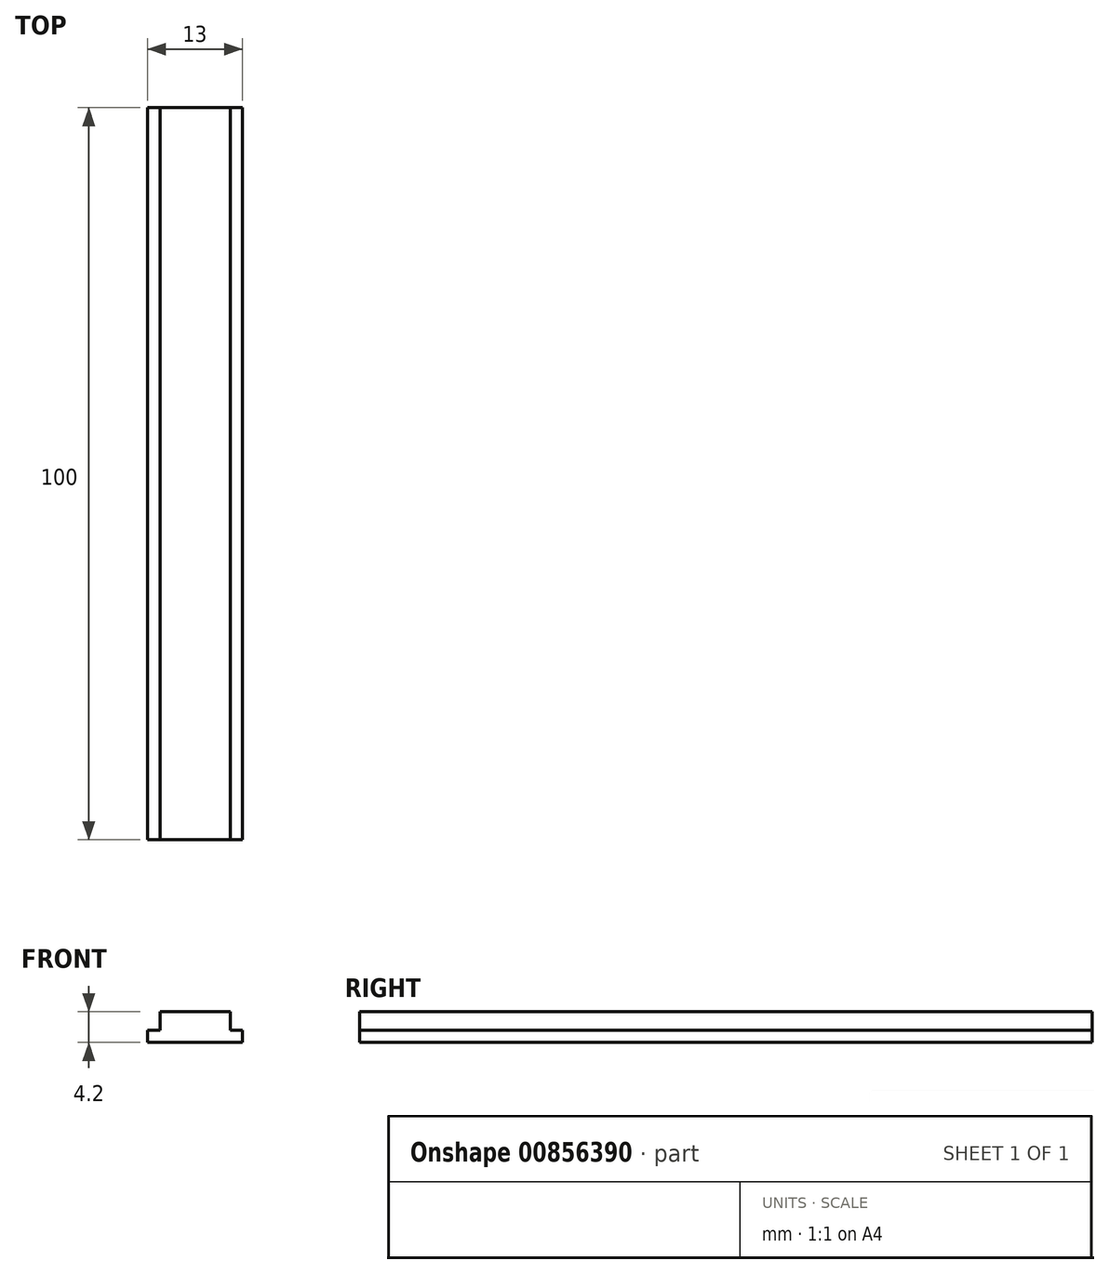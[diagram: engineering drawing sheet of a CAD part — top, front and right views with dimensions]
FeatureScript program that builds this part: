
annotation { "Feature Type Name" : "Feature", "Feature Type Description" : "" }
export const myFeature = defineFeature(function(context is Context, id is Id, definition is map)
    precondition{}
    {
        {
            var Q0;
            Q0=qCreatedBy(makeId("Front.planeOp"),FACE);
            var sketch = newSketch(context, id + "F0", { "sketchPlane" : qUnion([Q0])});
            skLineSegment(sketch, "E0", {"start": v(0.55, 2.47) * mm, "end": v(7.05, 2.47) * mm});
            skLineSegment(sketch, "E1", {"start": v(7.05, 2.47) * mm, "end": v(7.05, 4.17) * mm});
            skLineSegment(sketch, "E2", {"start": v(7.05, 4.17) * mm, "end": v(5.35, 4.17) * mm});
            skLineSegment(sketch, "E3", {"start": v(5.35, 4.17) * mm, "end": v(5.35, 6.67) * mm});
            skLineSegment(sketch, "E4", {"start": v(5.35, 6.67) * mm, "end": v(0.55, 6.67) * mm});
            skLineSegment(sketch, "E5.MirrorCS", {"start": v(-4.25, 6.67) * mm, "end": v(0.55, 6.67) * mm});
            skLineSegment(sketch, "E6.MirrorCS", {"start": v(-4.25, 4.17) * mm, "end": v(-4.25, 6.67) * mm});
            skLineSegment(sketch, "E7.MirrorCS", {"start": v(-5.95, 4.17) * mm, "end": v(-4.25, 4.17) * mm});
            skLineSegment(sketch, "E8.MirrorCS", {"start": v(-5.95, 2.47) * mm, "end": v(-5.95, 4.17) * mm});
            skLineSegment(sketch, "E9.MirrorCS", {"start": v(0.55, 2.47) * mm, "end": v(-5.95, 2.47) * mm});
            skSolve(sketch);
        }
        {
            var Q0;
            Q0 = qSketchRegion(id + "F0", true);
            extrude(context, id + "F1", {"entities" : qUnion([Q0]), "oppositeDirection" : true, "depth" : 100 * mm, "offsetDistance" : 25 * mm});
        }
    });
